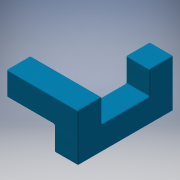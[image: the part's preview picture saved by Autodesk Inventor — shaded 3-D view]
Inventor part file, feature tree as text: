
AUTODESK INVENTOR PART (.ipt)
format: ipt  version: 2016 (Build 200138000, 138)  size: 169,472 bytes
history: native  units: in
note: dims shown in document units (in); Inventor stores cm internally (conversion verified against a paired STEP export)
features: plane x8, extrude x3, other x1, fillet x1, sketch x1
ambient origin geometry x8: Origin, YZ Plane, XZ Plane, XY Plane, X Axis, Y Axis, Z Axis, Center Point
bodies: Solid1 (feature_tree)
feature tree (14):
  other  "Cube Master.ipt"
  extrude  "Extrusion1"  Depth=0.3937in
  extrude  "Extrusion2"  Depth=0.0193in TaperAngle=0.0deg
  extrude  "Extrusion3"  Depth=0.0193in TaperAngle=0.0deg
  fillet  "Fillet1"  Radius=1.0in
  sketch  "Sketch1"  dims[d0=0.3937in d1=0.3937in d2=1.0in d3=0.0in d4=1.0in d5=0.0in d6=1.0in d7=0.0in d9=0.0193in d10=0.0193in]
  plane  "Work Plane1"
  plane  "Work Plane2"
  plane  "Work Plane3"
  plane  "Work Plane4"
  plane  "Work Plane5"
  plane  "Work Plane6"
  plane  "Work Plane7"
  plane  "Work Plane8"
